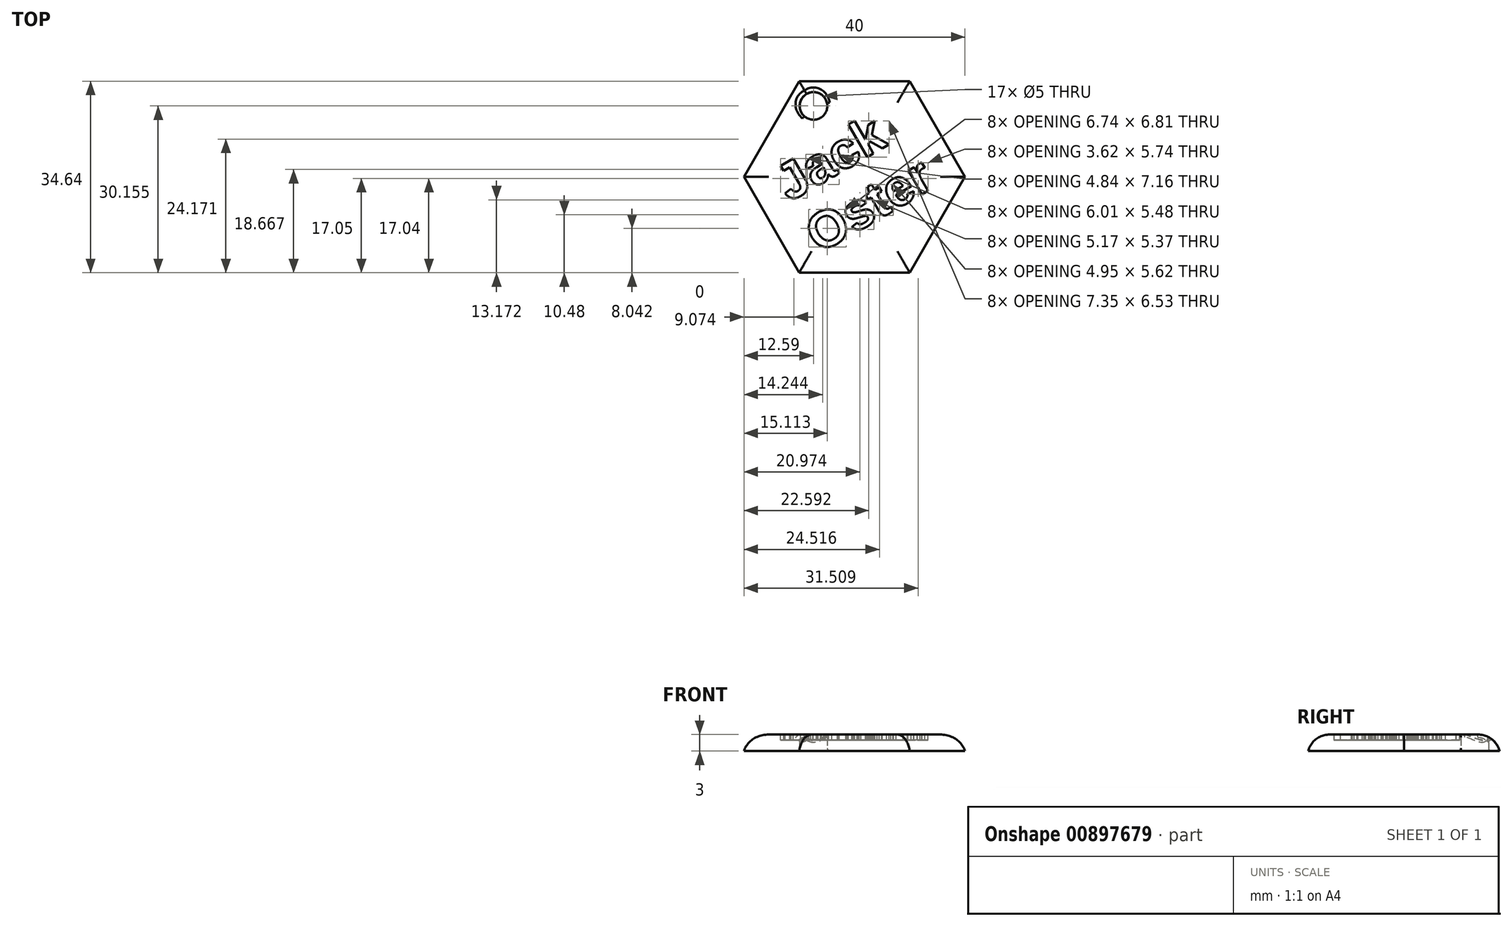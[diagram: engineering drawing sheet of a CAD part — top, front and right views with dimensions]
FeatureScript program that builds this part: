
annotation { "Feature Type Name" : "Feature", "Feature Type Description" : "" }
export const myFeature = defineFeature(function(context is Context, id is Id, definition is map)
    precondition{}
    {
        {
            var Q0;
            Q0=qCreatedBy(makeId("Top.planeOp"),FACE);
            var sketch = newSketch(context, id + "F0", { "sketchPlane" : qUnion([Q0])});
            skCircle(sketch, "E0.cCircle", {"center": v(0, 0) * mm, "radius": 17.32 * mm, "construction": true});
            skLineSegment(sketch, "E0.0", {"start": v(-10, 17.32) * mm, "end": v(10, 17.32) * mm});
            skLineSegment(sketch, "E0.1", {"start": v(10, 17.32) * mm, "end": v(20, 0) * mm});
            skLineSegment(sketch, "E0.2", {"start": v(20, 0) * mm, "end": v(10, -17.32) * mm});
            skLineSegment(sketch, "E0.3", {"start": v(10, -17.32) * mm, "end": v(-10, -17.32) * mm});
            skLineSegment(sketch, "E0.4", {"start": v(-10, -17.32) * mm, "end": v(-20, 0) * mm});
            skLineSegment(sketch, "E0.5", {"start": v(-20, 0) * mm, "end": v(-10, 17.32) * mm});
            skPoint(sketch, "E0.0.midPoint", {"position": v(0, 17.32) * mm});
            skLineSegment(sketch, "E1", {"start": v(0, 0) * mm, "end": v(-10, 17.32) * mm, "construction": true});
            skCircle(sketch, "E2", {"center": v(-7.41, 12.83) * mm, "radius": 2.5 * mm});
            skSolve(sketch);
        }
        {
            var Q0;
            Q0=makeQuery(id+"F0.imprint","IMPRINT",FACE,{"disambiguationData":[TD([[makeQuery(id+"F0.imprint","IMPRINT",EDGE,{"derivedFrom":sQuery(id+"F0.wireOp",EDGE,"E0.0")}),-1.0]])]});
            extrude(context, id + "F1", {"entities" : qUnion([Q0]), "depth" : 3 * mm, "offsetDistance" : 25 * mm});
        }
        {
            var Q0;
            Q0=makeQuery(id+"F1.opExtrude","CAP_FACE",FACE,{"disambiguationData":[OSD([sQuery(id+"F0.wireOp",EDGE,"E0.0"),sQuery(id+"F0.wireOp",EDGE,"E0.1"),sQuery(id+"F0.wireOp",EDGE,"E0.2"),sQuery(id+"F0.wireOp",EDGE,"E0.3"),sQuery(id+"F0.wireOp",EDGE,"E0.4"),sQuery(id+"F0.wireOp",EDGE,"E0.5"),sQuery(id+"F0.wireOp",EDGE,"E2")])],"isStart":false});
            var sketch = newSketch(context, id + "F2", { "sketchPlane" : qUnion([Q0])});
            skLineSegment(sketch, "E3", {"start": v(-10, 17.32) * mm, "end": v(0, 0) * mm, "construction": true});
            skText(sketch, "E4", { "text": "Jack\nOster", "fontName": "Arimo-Bold.ttf"});
            const initialGuessF2  = {"E4": [-0.0118, -0.00456, 0.86603, 0.5, 0.00675]};
            skSetInitialGuess(sketch, initialGuessF2);
            skSolve(sketch);
        }
        {
            var Q0;
            Q0 = qSketchRegion(id + "F2", true);
            extrude(context, id + "F3", {"entities" : qUnion([Q0]), "operationType" : NewBodyOperationType.REMOVE, "oppositeDirection" : true, "depth" : 1 * mm, "offsetDistance" : 25 * mm});
        }
        {
            var Q0;
            Q0=makeQuery(id+"F1.opExtrude","CAP_EDGE",EDGE,{"disambiguationData":[OSD([sQuery(id+"F0.wireOp",EDGE,"E0.4")])],"isStart":false});
            var Q1;
            Q1=makeQuery(id+"F1.opExtrude","CAP_EDGE",EDGE,{"disambiguationData":[OSD([sQuery(id+"F0.wireOp",EDGE,"E0.5")])],"isStart":false});
            var Q2;
            Q2=makeQuery(id+"F1.opExtrude","CAP_EDGE",EDGE,{"disambiguationData":[OSD([sQuery(id+"F0.wireOp",EDGE,"E0.0")])],"isStart":false});
            var Q3;
            Q3=makeQuery(id+"F1.opExtrude","CAP_EDGE",EDGE,{"disambiguationData":[OSD([sQuery(id+"F0.wireOp",EDGE,"E0.1")])],"isStart":false});
            var Q4;
            Q4=makeQuery(id+"F1.opExtrude","CAP_EDGE",EDGE,{"disambiguationData":[OSD([sQuery(id+"F0.wireOp",EDGE,"E0.2")])],"isStart":false});
            var Q5;
            Q5=makeQuery(id+"F1.opExtrude","CAP_EDGE",EDGE,{"disambiguationData":[OSD([sQuery(id+"F0.wireOp",EDGE,"E0.3")])],"isStart":false});
            fillet(context, id + "F4", {"entities" : qUnion([Q0, Q1, Q2, Q3, Q4, Q5]), "radius" : 4 * mm, "tangentPropagation" : true, "allowEdgeOverflow" : false});
        }
        {
            var Q0;
            Q0=makeQuery(id+"F4.opFillet","BLEND_EDGE",EDGE,{"blendedFrom":[makeQuery(id+"F1.opExtrude","CAP_EDGE",EDGE,{"disambiguationData":[OSD([sQuery(id+"F0.wireOp",EDGE,"E0.5")])],"isStart":false}),makeQuery(id+"F1.opExtrude","SWEPT_FACE",FACE,{"disambiguationData":[OSD([sQuery(id+"F0.wireOp",EDGE,"E2")])]})],"blendedInto":[makeQuery(id+"F1.opExtrude","SWEPT_FACE",FACE,{"disambiguationData":[OSD([sQuery(id+"F0.wireOp",EDGE,"E2")])]})]});
            var Q1;
            Q1=makeQuery(id+"F1.opExtrude","CAP_EDGE",EDGE,{"disambiguationData":[OSD([sQuery(id+"F0.wireOp",EDGE,"E2")])],"isStart":false});
            var Q2;
            Q2=makeQuery(id+"F1.opExtrude","CAP_EDGE",EDGE,{"disambiguationData":[OSD([sQuery(id+"F0.wireOp",EDGE,"E2")])],"isStart":true});
            fillet(context, id + "F5", {"entities" : qUnion([Q0, Q1, Q2]), "radius" : .5 * mm, "tangentPropagation" : true, "allowEdgeOverflow" : false});
        }
    });
